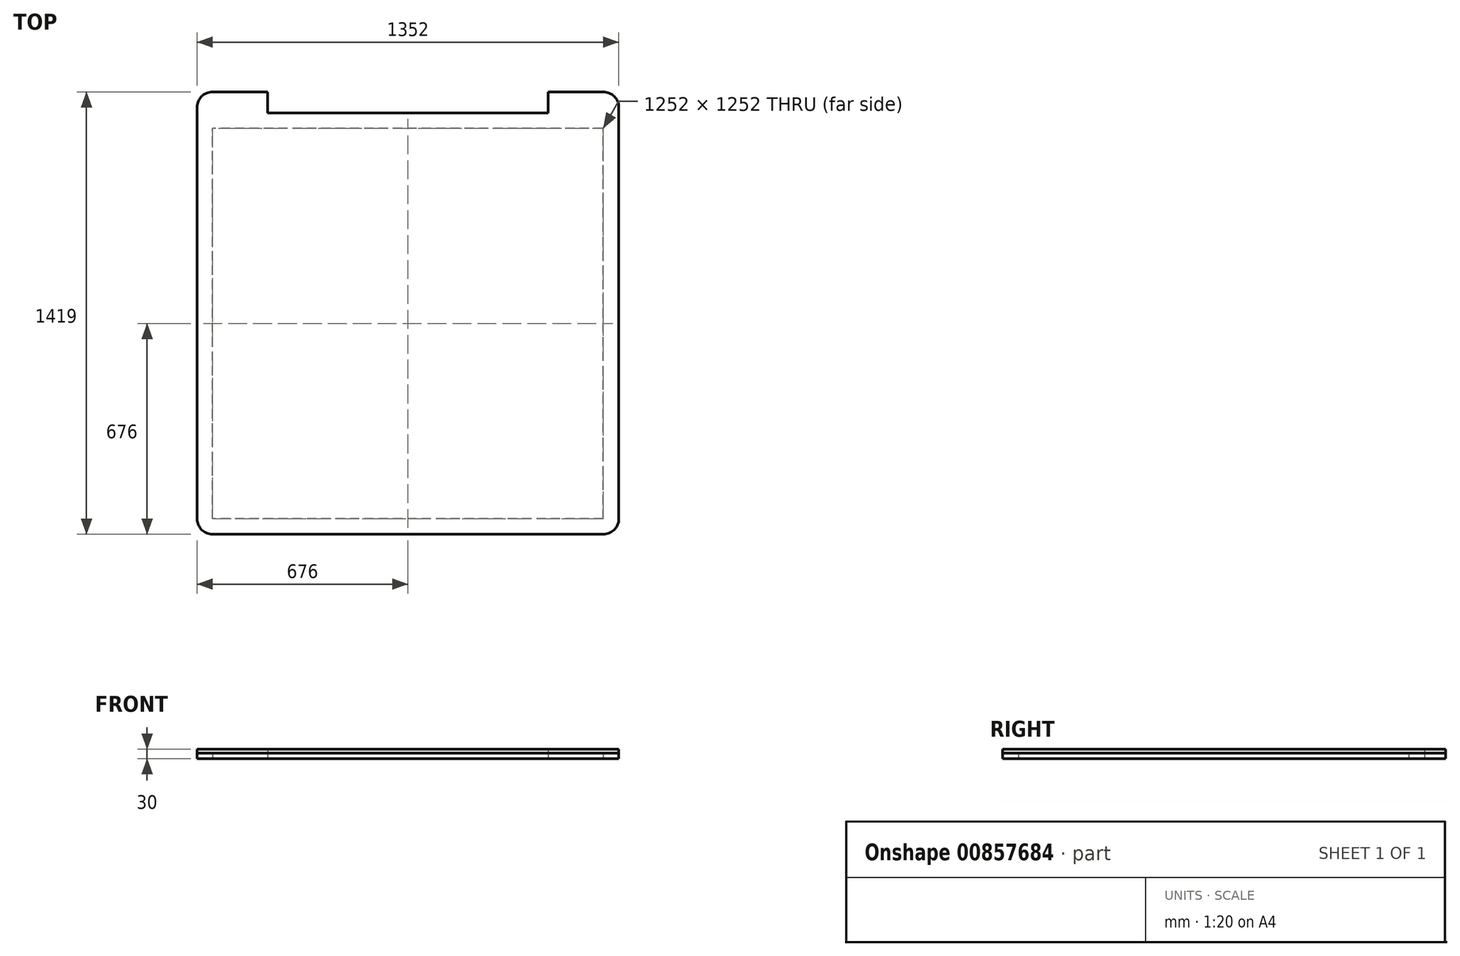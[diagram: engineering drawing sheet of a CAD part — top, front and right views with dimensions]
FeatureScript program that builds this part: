
annotation { "Feature Type Name" : "Feature", "Feature Type Description" : "" }
export const myFeature = defineFeature(function(context is Context, id is Id, definition is map)
    precondition{}
    {
        {
            var Q0;
            Q0=qCreatedBy(makeId("Top.planeOp"),FACE);
            var sketch = newSketch(context, id + "F0", { "sketchPlane" : qUnion([Q0])});
            skLineSegment(sketch, "E0.bottom", {"start": v(626, -676) * mm, "end": v(-626, -676) * mm});
            skLineSegment(sketch, "E0.top", {"start": v(450, 676) * mm, "end": v(-450, 676) * mm});
            skLineSegment(sketch, "E0.left", {"start": v(676, -626) * mm, "end": v(676, 626) * mm});
            skLineSegment(sketch, "E0.right", {"start": v(-676, -626) * mm, "end": v(-676, 626) * mm});
            skPoint(sketch, "E0.middle", {"position": v(0, 0) * mm});
            skPoint(sketch, "E1.visualSharp", {"position": v(-676, 676) * mm});
            skPoint(sketch, "E2.visualSharp", {"position": v(676, 676) * mm});
            skPoint(sketch, "E3.visualSharp", {"position": v(676, -676) * mm});
            skArc(sketch, "E3.filletArc", {"start": v(626, -676) * mm, "mid": v(661.36, -661.36) * mm, "end": v(676, -626) * mm});
            skPoint(sketch, "E4.visualSharp", {"position": v(-676, -676) * mm});
            skArc(sketch, "E4.filletArc", {"start": v(-676, -626) * mm, "mid": v(-661.36, -661.36) * mm, "end": v(-626, -676) * mm});
            skLineSegment(sketch, "E5", {"start": v(-450, 676) * mm, "end": v(-450, 743) * mm});
            skLineSegment(sketch, "E6", {"start": v(-450, 743) * mm, "end": v(-626, 743) * mm});
            skLineSegment(sketch, "E7", {"start": v(-676, 626) * mm, "end": v(-676, 693) * mm});
            skPoint(sketch, "E8.newPointA", {"position": v(-670.1, 743) * mm});
            skPoint(sketch, "E8.newPointB", {"position": v(-676, 743) * mm});
            skArc(sketch, "E8.filletArc", {"start": v(-626, 743) * mm, "mid": v(-661.36, 728.36) * mm, "end": v(-676, 693) * mm});
            skLineSegment(sketch, "E9", {"start": v(676, 626) * mm, "end": v(676, 693) * mm});
            skLineSegment(sketch, "E10", {"start": v(626, 743) * mm, "end": v(450, 743) * mm});
            skLineSegment(sketch, "E11", {"start": v(450, 743) * mm, "end": v(450, 676) * mm});
            skPoint(sketch, "E12.visualSharp", {"position": v(676, 743) * mm});
            skArc(sketch, "E12.filletArc", {"start": v(676, 693) * mm, "mid": v(661.36, 728.36) * mm, "end": v(626, 743) * mm});
            skSolve(sketch);
        }
        {
            var Q0;
            Q0=makeQuery(id+"F0.imprint","IMPRINT",FACE,{"disambiguationData":[TD([[makeQuery(id+"F0.imprint","IMPRINT",EDGE,{"derivedFrom":sQuery(id+"F0.wireOp",EDGE,"E0.bottom")}),-1.0]])]});
            extrude(context, id + "F1", {"entities" : qUnion([Q0]), "depth" : 18 * mm, "offsetDistance" : 25 * mm});
        }
        {
            var Q0;
            Q0=makeQuery(id+"F1.opExtrude","CAP_FACE",FACE,{"disambiguationData":[OSD([sQuery(id+"F0.wireOp",EDGE,"E0.bottom"),sQuery(id+"F0.wireOp",EDGE,"E0.top"),sQuery(id+"F0.wireOp",EDGE,"E0.left"),sQuery(id+"F0.wireOp",EDGE,"E0.right"),sQuery(id+"F0.wireOp",EDGE,"E1.filletArc"),sQuery(id+"F0.wireOp",EDGE,"E2.filletArc"),sQuery(id+"F0.wireOp",EDGE,"E3.filletArc"),sQuery(id+"F0.wireOp",EDGE,"E4.filletArc")])],"isStart":false});
            extrude(context, id + "F2", {"entities" : qUnion([Q0]), "depth" : 12 * mm, "offsetDistance" : 25 * mm});
        }
        {
            var Q0;
            Q0=makeQuery(id+"F1.opExtrude","CAP_FACE",FACE,{"disambiguationData":[OSD([sQuery(id+"F0.wireOp",EDGE,"E0.bottom"),sQuery(id+"F0.wireOp",EDGE,"E0.top"),sQuery(id+"F0.wireOp",EDGE,"E0.left"),sQuery(id+"F0.wireOp",EDGE,"E0.right"),sQuery(id+"F0.wireOp",EDGE,"E1.filletArc"),sQuery(id+"F0.wireOp",EDGE,"E2.filletArc"),sQuery(id+"F0.wireOp",EDGE,"E3.filletArc"),sQuery(id+"F0.wireOp",EDGE,"E4.filletArc")])],"isStart":true});
            var sketch = newSketch(context, id + "F3", { "sketchPlane" : qUnion([Q0])});
            skLineSegment(sketch, "E13.0", {"start": v(626, 626) * mm, "end": v(-626, 626) * mm});
            skLineSegment(sketch, "E13.1", {"start": v(626, 626) * mm, "end": v(626, -626) * mm});
            skLineSegment(sketch, "E13.2", {"start": v(626, -626) * mm, "end": v(-626, -626) * mm});
            skLineSegment(sketch, "E13.3", {"start": v(-626, 626) * mm, "end": v(-626, -626) * mm});
            skSolve(sketch);
        }
        {
            var Q0;
            Q0=makeQuery(id+"F3.imprint","IMPRINT",FACE,{"disambiguationData":[TD([[makeQuery(id+"F3.imprint","IMPRINT",EDGE,{"derivedFrom":sQuery(id+"F3.wireOp",EDGE,"E13.0")}),1.0]])]});
            extrude(context, id + "F4", {"entities" : qUnion([Q0]), "oppositeDirection" : true, "depth" : 18 * mm, "offsetDistance" : 25 * mm});
        }
        {
            var Q0;
            Q0=makeQuery(id+"F4.opExtrude","SWEPT_BODY",BODY,{"disambiguationData":[OSD([sQuery(id+"F3.wireOp",EDGE,"E13.0"),sQuery(id+"F3.wireOp",EDGE,"E13.1"),sQuery(id+"F3.wireOp",EDGE,"E13.2"),sQuery(id+"F3.wireOp",EDGE,"E13.3")])]});
            var Q1;
            Q1=makeQuery(id+"F1.opExtrude","SWEPT_BODY",BODY,{"disambiguationData":[OSD([sQuery(id+"F0.wireOp",EDGE,"E0.bottom"),sQuery(id+"F0.wireOp",EDGE,"E0.top"),sQuery(id+"F0.wireOp",EDGE,"E0.left"),sQuery(id+"F0.wireOp",EDGE,"E0.right"),sQuery(id+"F0.wireOp",EDGE,"E1.filletArc"),sQuery(id+"F0.wireOp",EDGE,"E2.filletArc"),sQuery(id+"F0.wireOp",EDGE,"E3.filletArc"),sQuery(id+"F0.wireOp",EDGE,"E4.filletArc")])]});
            booleanBodies(context, id + "F5", {"operationType" : BooleanOperationType.SUBTRACTION, "tools" : qUnion([Q0]), "targets" : qUnion([Q1]), "keepTools" : true});
        }
    });
